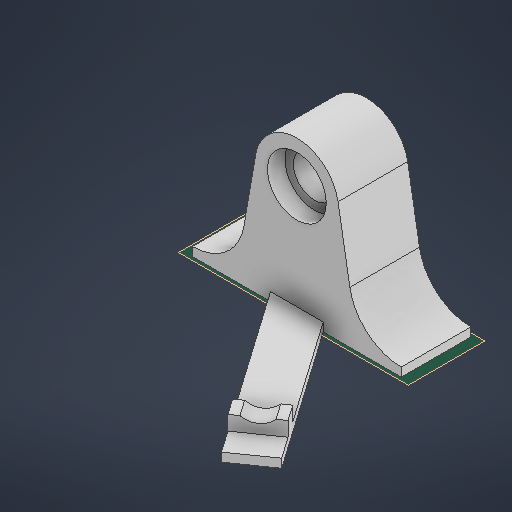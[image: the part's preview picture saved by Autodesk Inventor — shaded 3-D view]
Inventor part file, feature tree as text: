
AUTODESK INVENTOR PART (.ipt)
format: ipt  version: 2025.3 (Build 293356030, 356C)  size: 273,920 bytes
history: native  units: mm
features: extrude x7, sketch x3, plane x1, projected_geometry x1
ambient origin geometry x8: Origin, YZ Plane, XZ Plane, XY Plane, X Axis, Y Axis, Z Axis, Center Point
bodies: Solid1 (feature_tree)
feature tree (12):
  sketch  "Sketch1"  dims[d0=16.9mm d1=12.0mm d2=30.0mm d3=12.0mm d4=15.0mm d5=60.0mm d6=2.5mm d7=20.0mm d8=0.0mm]
  extrude  "Extrusion1"  Depth=20.0mm TaperAngle=0.0deg
  extrude  "Extrusion2"  Depth=20.0mm TaperAngle=0.0deg
  extrude  "Extrusion3"  Depth=7.5mm
  plane  "Work Plane1"
  sketch  "Sketch2"  dims[d9=15.0mm d10=0.0mm d11=20.0mm d12=0.0mm]
  extrude  "Extrusion6"  Depth=5.5mm
  sketch  "Sketch4"  dims[d13=0.0mm d14=6.108652mm d16=5.5mm d17=20.0mm d26=40.0mm d27=2.5mm d28=0.0mm d29=14.6mm d30=10.7mm d31=1.5mm d32=8.0mm d33=5.5mm d34=0.0mm d35=5.5mm d36=0.0mm d37=7.5mm d38=0.0mm]
  extrude  "Extrusion7"  Depth=20.0mm
  extrude  "Extrusion8"  Depth=7.5mm
  extrude  "Extrusion9"  Depth=2.5mm TaperAngle=0.0deg
  projected_geometry  "Projected Loop2"
